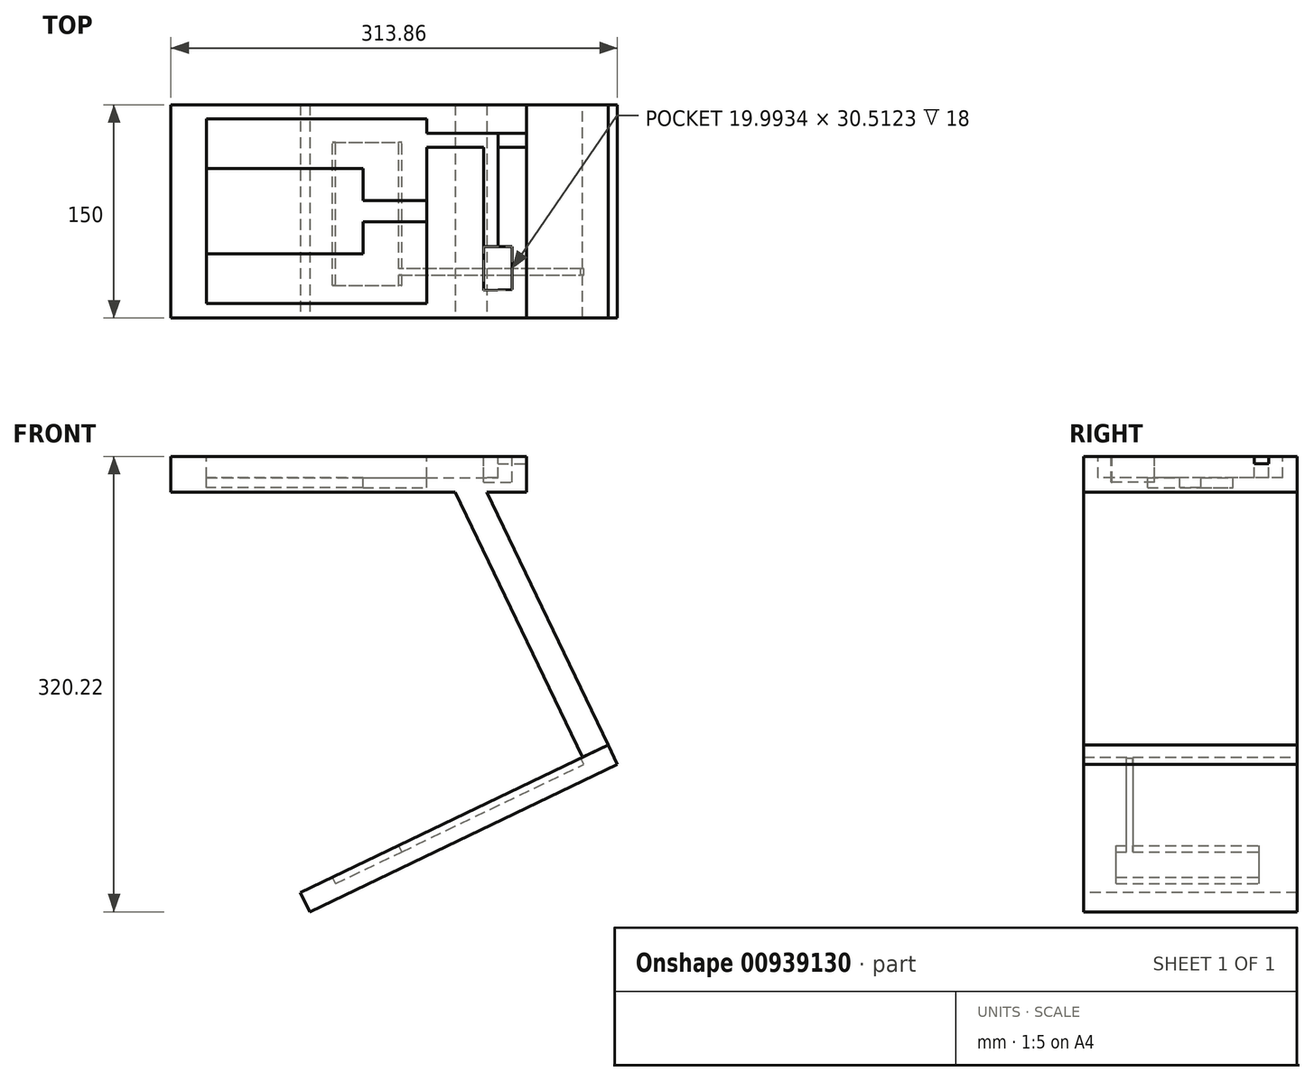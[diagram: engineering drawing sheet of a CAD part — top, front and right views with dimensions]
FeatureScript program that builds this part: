
annotation { "Feature Type Name" : "Feature", "Feature Type Description" : "" }
export const myFeature = defineFeature(function(context is Context, id is Id, definition is map)
    precondition{}
    {
        {
            var Q0;
            Q0=qCreatedBy(makeId("Top.planeOp"),FACE);
            var sketch = newSketch(context, id + "F0", { "sketchPlane" : qUnion([Q0])});
            skLineSegment(sketch, "E0.bottom", {"start": v(125, 75) * mm, "end": v(-125, 75) * mm});
            skLineSegment(sketch, "E0.top", {"start": v(125, -75) * mm, "end": v(-125, -75) * mm});
            skLineSegment(sketch, "E0.left", {"start": v(125, 75) * mm, "end": v(125, -75) * mm});
            skLineSegment(sketch, "E0.right", {"start": v(-125, 75) * mm, "end": v(-125, -75) * mm});
            skPoint(sketch, "E0.middle", {"position": v(0, 0) * mm});
            skLineSegment(sketch, "E1.bottom", {"start": v(10, -30) * mm, "end": v(-100, -30) * mm});
            skLineSegment(sketch, "E1.top", {"start": v(10, 30) * mm, "end": v(-100, 30) * mm});
            skLineSegment(sketch, "E1.left", {"start": v(10, -30) * mm, "end": v(10, -7.5) * mm});
            skLineSegment(sketch, "E1.right", {"start": v(-100, -30) * mm, "end": v(-100, 30) * mm});
            skPoint(sketch, "E1.middle", {"position": v(-45, 0) * mm});
            skLineSegment(sketch, "E2", {"start": v(-45, 0) * mm, "end": v(-125, 0) * mm, "construction": true});
            skLineSegment(sketch, "E3.bottom", {"start": v(-100, 65) * mm, "end": v(55, 65) * mm});
            skLineSegment(sketch, "E3.top", {"start": v(-100, -65) * mm, "end": v(55, -65) * mm});
            skLineSegment(sketch, "E3.left", {"start": v(-100, 65) * mm, "end": v(-100, -65) * mm});
            skLineSegment(sketch, "E3.right", {"start": v(55, 65) * mm, "end": v(55, -65) * mm});
            skLineSegment(sketch, "E4", {"start": v(10, 7.5) * mm, "end": v(55, 7.5) * mm});
            skLineSegment(sketch, "E5", {"start": v(10, -7.5) * mm, "end": v(55, -7.5) * mm});
            skLineSegment(sketch, "E6.trimOffspring", {"start": v(10, 7.5) * mm, "end": v(10, 30) * mm});
            skLineSegment(sketch, "E7", {"start": v(55, 55) * mm, "end": v(125, 55) * mm});
            skLineSegment(sketch, "E8", {"start": v(61.74, 55) * mm, "end": v(61.74, 75) * mm, "construction": true});
            skLineSegment(sketch, "E9", {"start": v(55, 45) * mm, "end": v(125, 45) * mm});
            skLineSegment(sketch, "E10", {"start": v(95, 45) * mm, "end": v(95, 55) * mm, "construction": true});
            skLineSegment(sketch, "E11", {"start": v(105, 45) * mm, "end": v(105, -25) * mm});
            skLineSegment(sketch, "E12", {"start": v(105, -25) * mm, "end": v(115, -25) * mm});
            skLineSegment(sketch, "E13", {"start": v(115, -25) * mm, "end": v(115, -55) * mm});
            skLineSegment(sketch, "E14", {"start": v(95, 45) * mm, "end": v(95, -55.51) * mm});
            skLineSegment(sketch, "E15", {"start": v(95, -55.51) * mm, "end": v(115, -55) * mm});
            skLineSegment(sketch, "E16", {"start": v(105, -25) * mm, "end": v(95, -25) * mm});
            skLineSegment(sketch, "E17", {"start": v(125, 8.04) * mm, "end": v(105, 8.04) * mm, "construction": true});
            skLineSegment(sketch, "E18", {"start": v(105, 45) * mm, "end": v(105, 55) * mm});
            skSolve(sketch);
        }
        {
            var Q0;
            Q0=makeQuery(id+"F0.imprint","IMPRINT",FACE,{"disambiguationData":[TD([[makeQuery(id+"F0.imprint","IMPRINT",EDGE,{"derivedFrom":sQuery(id+"F0.wireOp",EDGE,"E0.bottom")}),1.0]])]});
            var Q1;
            {var subQ2=sQuery(id+"F0.wireOp",EDGE,"E1.bottom");Q1=makeQuery(id+"F0.imprint","IMPRINT",FACE,{"disambiguationData":[TD([[makeQuery(id+"F0.imprint","IMPRINT",EDGE,{"derivedFrom":subQ2}),1.0]])]});}
            var Q2;
            {var subQ0=sQuery(id+"F0.wireOp",EDGE,"E1.bottom");Q2=makeQuery(id+"F0.imprint","IMPRINT",FACE,{"disambiguationData":[TD([[makeQuery(id+"F0.imprint","IMPRINT",EDGE,{"derivedFrom":subQ0}),-1.0]])]});}
            var Q3;
            {var subQ1=sQuery(id+"F0.wireOp",EDGE,"E1.top");Q3=makeQuery(id+"F0.imprint","IMPRINT",FACE,{"disambiguationData":[TD([[makeQuery(id+"F0.imprint","IMPRINT",EDGE,{"derivedFrom":subQ1}),-1.0]])]});}
            var Q4;
            {var subQ0=sQuery(id+"F0.wireOp",EDGE,"E11");Q4=makeQuery(id+"F0.imprint","IMPRINT",FACE,{"disambiguationData":[TD([[makeQuery(id+"F0.imprint","IMPRINT",EDGE,{"derivedFrom":subQ0}),-1.0]])]});}
            var Q5;
            {var subQ0=sQuery(id+"F0.wireOp",EDGE,"E7");Q5=makeQuery(id+"F0.imprint","IMPRINT",FACE,{"disambiguationData":[TD([[makeQuery(id+"F0.imprint","IMPRINT",EDGE,{"derivedFrom":subQ0}),-1.0]])]});}
            var Q6;
            Q6=makeQuery(id+"F0.imprint","IMPRINT",FACE,{"disambiguationData":[TD([[makeQuery(id+"F0.imprint","IMPRINT",EDGE,{"derivedFrom":sQuery(id+"F0.wireOp",EDGE,"E12")}),-1.0]])]});
            var Q7;
            {var subQ6=sQuery(id+"F0.wireOp",EDGE,"E18");Q7=makeQuery(id+"F0.imprint","IMPRINT",FACE,{"disambiguationData":[TD([[makeQuery(id+"F0.imprint","IMPRINT",EDGE,{"derivedFrom":subQ6}),1.0]])]});}
            extrude(context, id + "F1", {"entities" : qUnion([Q0, Q1, Q2, Q3, Q4, Q5, Q6, Q7]), "oppositeDirection" : true, "depth" : 25 * mm, "offsetDistance" : 25 * mm});
        }
        {
            var Q0;
            {var subQ2=sQuery(id+"F0.wireOp",EDGE,"E1.bottom");Q0=makeQuery(id+"F0.imprint","IMPRINT",FACE,{"disambiguationData":[TD([[makeQuery(id+"F0.imprint","IMPRINT",EDGE,{"derivedFrom":subQ2}),1.0]])]});}
            var Q1;
            {var subQ0=sQuery(id+"F0.wireOp",EDGE,"E1.bottom");Q1=makeQuery(id+"F0.imprint","IMPRINT",FACE,{"disambiguationData":[TD([[makeQuery(id+"F0.imprint","IMPRINT",EDGE,{"derivedFrom":subQ0}),-1.0]])]});}
            var Q2;
            {var subQ1=sQuery(id+"F0.wireOp",EDGE,"E1.top");Q2=makeQuery(id+"F0.imprint","IMPRINT",FACE,{"disambiguationData":[TD([[makeQuery(id+"F0.imprint","IMPRINT",EDGE,{"derivedFrom":subQ1}),-1.0]])]});}
            extrude(context, id + "F2", {"entities" : qUnion([Q0, Q1, Q2]), "operationType" : NewBodyOperationType.REMOVE, "oppositeDirection" : true, "depth" : 15 * mm, "offsetDistance" : 25 * mm});
        }
        {
            var Q0;
            {var subQ0=sQuery(id+"F0.wireOp",EDGE,"E1.bottom");Q0=makeQuery(id+"F0.imprint","IMPRINT",FACE,{"disambiguationData":[TD([[makeQuery(id+"F0.imprint","IMPRINT",EDGE,{"derivedFrom":subQ0}),-1.0]])]});}
            extrude(context, id + "F3", {"entities" : qUnion([Q0]), "operationType" : NewBodyOperationType.REMOVE, "oppositeDirection" : true, "depth" : 22 * mm, "offsetDistance" : 25 * mm});
        }
        {
            var Q0;
            Q0=makeQuery(id+"F1.opExtrude","SWEPT_FACE",FACE,{"disambiguationData":[OSD([sQuery(id+"F0.wireOp",EDGE,"E0.top")])]});
            var sketch = newSketch(context, id + "F4", { "sketchPlane" : qUnion([Q0])});
            skLineSegment(sketch, "E19.0.0", {"start": v(125, 0) * mm, "end": v(-125, 0) * mm});
            skLineSegment(sketch, "E19.0.1", {"start": v(-125, 0) * mm, "end": v(-125, -25) * mm});
            skLineSegment(sketch, "E19.0.2", {"start": v(-125, -25) * mm, "end": v(125, -25) * mm});
            skLineSegment(sketch, "E19.0.3", {"start": v(125, -25) * mm, "end": v(125, 0) * mm});
            skLineSegment(sketch, "E20", {"start": v(85, 0) * mm, "end": v(97, -25) * mm});
            skLineSegment(sketch, "E21", {"start": v(62.82, 0) * mm, "end": v(74.82, -25) * mm});
            skSolve(sketch);
        }
        {
            var Q0;
            {var subQ0=sQuery(id+"F4.wireOp",EDGE,"E20");Q0=makeQuery(id+"F4.imprint","IMPRINT",FACE,{"disambiguationData":[TD([[makeQuery(id+"F4.imprint","IMPRINT",EDGE,{"derivedFrom":subQ0}),-1.0]])]});}
            extrude(context, id + "F5", {"entities" : qUnion([Q0]), "operationType" : NewBodyOperationType.REMOVE, "oppositeDirection" : true, "depth" : 80 * mm, "offsetDistance" : 25 * mm});
        }
        {
            var Q0;
            Q0=makeQuery(id+"F5.boolean.opBoolean","COPY",FACE,{"derivedFrom":makeQuery(id+"F5.opExtrude","CAP_FACE",FACE,{"disambiguationData":[OSD([sQuery(id+"F4.wireOp",EDGE,"E19.0.0"),sQuery(id+"F4.wireOp",EDGE,"E19.0.2"),sQuery(id+"F4.wireOp",EDGE,"E20"),sQuery(id+"F4.wireOp",EDGE,"E21")])],"isStart":false})});
            var sketch = newSketch(context, id + "F6", { "sketchPlane" : qUnion([Q0])});
            skLineSegment(sketch, "E22.0", {"start": v(62.82, 0) * mm, "end": v(74.82, -25) * mm});
            skLineSegment(sketch, "E23.0", {"start": v(85, 0) * mm, "end": v(97, -25) * mm});
            skLineSegment(sketch, "E24", {"start": v(85, 0) * mm, "end": v(62.82, 0) * mm});
            skLineSegment(sketch, "E25", {"start": v(97, -25) * mm, "end": v(182.36, -202.84) * mm});
            skLineSegment(sketch, "E26", {"start": v(74.82, -25) * mm, "end": v(164.33, -211.5) * mm});
            skLineSegment(sketch, "E27", {"start": v(97, -25) * mm, "end": v(74.82, -25) * mm});
            skLineSegment(sketch, "E28", {"start": v(182.36, -202.84) * mm, "end": v(164.33, -211.5) * mm});
            skSolve(sketch);
        }
        {
            var Q0;
            Q0=makeQuery(id+"F6.imprint","IMPRINT",FACE,{"disambiguationData":[TD([[makeQuery(id+"F6.imprint","IMPRINT",EDGE,{"derivedFrom":sQuery(id+"F6.wireOp",EDGE,"E23.0")}),-1.0]])]});
            var Q1;
            Q1=makeQuery(id+"F6.imprint","IMPRINT",FACE,{"disambiguationData":[TD([[makeQuery(id+"F6.imprint","IMPRINT",EDGE,{"derivedFrom":sQuery(id+"F6.wireOp",EDGE,"E25")}),-1.0]])]});
            var Q2;
            {var subQ0=sQuery(id+"F0.wireOp",EDGE,"E0.right");var subQ2=sQuery(id+"F0.wireOp",EDGE,"E0.top");Q2=makeQuery(id+"F5.boolean.opBoolean","SPLIT",FACE,{"disambiguationData":[TD([makeQuery(id+"F1.opExtrude","SWEPT_FACE",FACE,{"disambiguationData":[OSD([subQ0])]})])],"derivedFrom":makeQuery(id+"F1.opExtrude","SWEPT_FACE",FACE,{"disambiguationData":[OSD([subQ2])]})});}
            extrude(context, id + "F7", {"entities" : qUnion([Q0, Q1]), "endBound" : BoundingType.UP_TO_SURFACE, "depth" : 25 * mm, "endBoundEntityFace" : qUnion([Q2]), "offsetDistance" : 25 * mm});
        }
        {
            var Q0;
            Q0=makeQuery(id+"F6.imprint","IMPRINT",FACE,{"disambiguationData":[TD([[makeQuery(id+"F6.imprint","IMPRINT",EDGE,{"derivedFrom":sQuery(id+"F6.wireOp",EDGE,"E25")}),-1.0]])]});
            var Q1;
            Q1=makeQuery(id+"F1.opExtrude","SWEPT_FACE",FACE,{"disambiguationData":[OSD([sQuery(id+"F0.wireOp",EDGE,"E0.bottom")])]});
            extrude(context, id + "F8", {"entities" : qUnion([Q0]), "operationType" : NewBodyOperationType.ADD, "endBound" : BoundingType.UP_TO_SURFACE, "oppositeDirection" : true, "depth" : 25 * mm, "endBoundEntityFace" : qUnion([Q1]), "offsetDistance" : 25 * mm});
        }
        {
            var Q0;
            Q0=makeQuery(id+"F7.opExtrude","CAP_FACE",FACE,{"disambiguationData":[OSD([sQuery(id+"F6.wireOp",EDGE,"E22.0"),sQuery(id+"F6.wireOp",EDGE,"E23.0"),sQuery(id+"F6.wireOp",EDGE,"E24"),sQuery(id+"F6.wireOp",EDGE,"E25"),sQuery(id+"F6.wireOp",EDGE,"E26"),sQuery(id+"F6.wireOp",EDGE,"t3HZJVrx-LeC2-CU6D-Bioz-bMVZM4buclfs")])],"isStart":false});
            var sketch = newSketch(context, id + "F9", { "sketchPlane" : qUnion([Q0])});
            skLineSegment(sketch, "E29.0", {"start": v(182.36, -202.84) * mm, "end": v(164.33, -211.5) * mm});
            skLineSegment(sketch, "E30", {"start": v(164.33, -211.5) * mm, "end": v(-34, -306.7) * mm});
            skLineSegment(sketch, "E31", {"start": v(182.36, -202.84) * mm, "end": v(188.86, -216.37) * mm});
            skLineSegment(sketch, "E32", {"start": v(-34, -306.7) * mm, "end": v(-27.51, -320.22) * mm});
            skLineSegment(sketch, "E33", {"start": v(188.86, -216.37) * mm, "end": v(-27.51, -320.22) * mm});
            skSolve(sketch);
        }
        {
            var Q0;
            Q0=makeQuery(id+"F9.imprint","IMPRINT",FACE,{"disambiguationData":[TD([[makeQuery(id+"F9.imprint","IMPRINT",EDGE,{"derivedFrom":sQuery(id+"F9.wireOp",EDGE,"E29.0")}),-1.0]])]});
            extrude(context, id + "F10", {"entities" : qUnion([Q0]), "oppositeDirection" : true, "depth" : 150 * mm, "offsetDistance" : 25 * mm});
        }
        {
            var Q0;
            Q0=makeQuery(id+"F10.opExtrude","SWEPT_FACE",FACE,{"disambiguationData":[OSD([sQuery(id+"F9.wireOp",EDGE,"E29.0"),sQuery(id+"F9.wireOp",EDGE,"E30")])]});
            var sketch = newSketch(context, id + "F11", { "sketchPlane" : qUnion([Q0])});
            skLineSegment(sketch, "E34", {"start": v(-163.37, 0) * mm, "end": v(76.63, 0) * mm, "construction": true});
            skLineSegment(sketch, "E35.bottom", {"start": v(-138.43, -52.03) * mm, "end": v(-86.71, -52.03) * mm});
            skLineSegment(sketch, "E35.top", {"start": v(-138.43, 48.63) * mm, "end": v(-86.71, 48.63) * mm});
            skLineSegment(sketch, "E35.left", {"start": v(-138.43, -52.03) * mm, "end": v(-138.43, 48.63) * mm});
            skLineSegment(sketch, "E35.right", {"start": v(-86.71, -52.03) * mm, "end": v(-86.71, 48.63) * mm});
            skLineSegment(sketch, "E36", {"start": v(-86.71, -45) * mm, "end": v(55.33, -45) * mm});
            skLineSegment(sketch, "E37", {"start": v(55.33, -45) * mm, "end": v(55.33, -40.52) * mm});
            skLineSegment(sketch, "E38", {"start": v(55.33, -40.52) * mm, "end": v(-86.71, -40.52) * mm});
            skSolve(sketch);
        }
        {
            var Q0;
            Q0 = qSketchRegion(id + "F11", true);
            extrude(context, id + "F12", {"entities" : qUnion([Q0]), "operationType" : NewBodyOperationType.REMOVE, "oppositeDirection" : true, "depth" : 5 * mm, "offsetDistance" : 25 * mm});
        }
        {
            var Q0;
            {var subQ0=sQuery(id+"F0.wireOp",EDGE,"E11");Q0=makeQuery(id+"F0.imprint","IMPRINT",FACE,{"disambiguationData":[TD([[makeQuery(id+"F0.imprint","IMPRINT",EDGE,{"derivedFrom":subQ0}),-1.0]])]});}
            extrude(context, id + "F13", {"entities" : qUnion([Q0]), "operationType" : NewBodyOperationType.REMOVE, "oppositeDirection" : true, "depth" : 15 * mm, "offsetDistance" : 25 * mm});
        }
        {
            var Q0;
            Q0=makeQuery(id+"F0.imprint","IMPRINT",FACE,{"disambiguationData":[TD([[makeQuery(id+"F0.imprint","IMPRINT",EDGE,{"derivedFrom":sQuery(id+"F0.wireOp",EDGE,"E12")}),-1.0]])]});
            extrude(context, id + "F14", {"entities" : qUnion([Q0]), "operationType" : NewBodyOperationType.REMOVE, "oppositeDirection" : true, "depth" : 18 * mm, "offsetDistance" : 25 * mm});
        }
        {
            var Q0;
            {var subQ6=sQuery(id+"F0.wireOp",EDGE,"E18");Q0=makeQuery(id+"F0.imprint","IMPRINT",FACE,{"disambiguationData":[TD([[makeQuery(id+"F0.imprint","IMPRINT",EDGE,{"derivedFrom":subQ6}),1.0]])]});}
            extrude(context, id + "F15", {"entities" : qUnion([Q0]), "operationType" : NewBodyOperationType.REMOVE, "oppositeDirection" : true, "depth" : 15 * mm, "offsetDistance" : 25 * mm});
        }
        {
            var Q0;
            {var subQ5=sQuery(id+"F0.wireOp",EDGE,"E18");Q0=makeQuery(id+"F0.imprint","IMPRINT",FACE,{"disambiguationData":[TD([[makeQuery(id+"F0.imprint","IMPRINT",EDGE,{"derivedFrom":subQ5}),-1.0]])]});}
            extrude(context, id + "F16", {"entities" : qUnion([Q0]), "operationType" : NewBodyOperationType.REMOVE, "oppositeDirection" : true, "depth" : 5 * mm, "offsetDistance" : 25 * mm});
        }
    });
